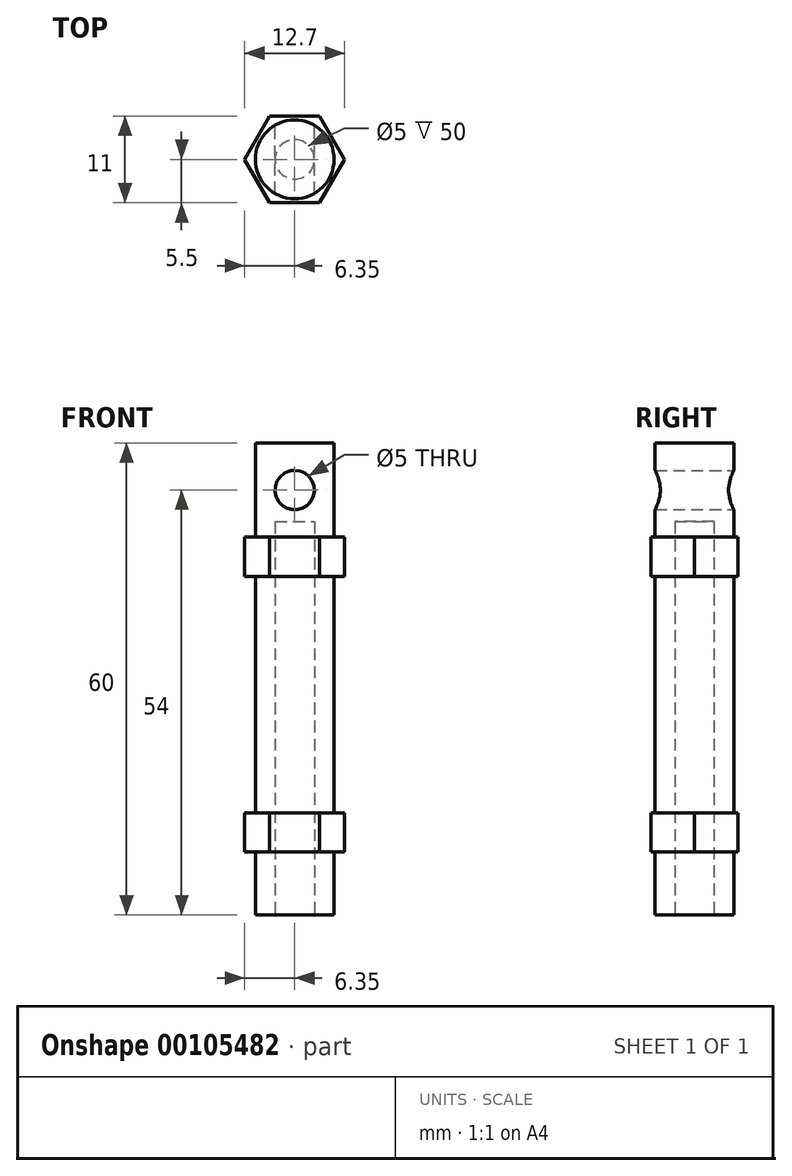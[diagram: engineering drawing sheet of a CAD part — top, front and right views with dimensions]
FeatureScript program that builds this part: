
annotation { "Feature Type Name" : "Feature", "Feature Type Description" : "" }
export const myFeature = defineFeature(function(context is Context, id is Id, definition is map)
    precondition{}
    {
        {
            var Q0;
            Q0=qCreatedBy(makeId("Top.planeOp"),FACE);
            var sketch = newSketch(context, id + "F0", { "sketchPlane" : qUnion([Q0])});
            skCircle(sketch, "E0", {"center": v(0, 0) * mm, "radius": 5 * mm});
            skSolve(sketch);
        }
        {
            var Q0;
            Q0=makeQuery(id+"F0.imprint","IMPRINT",FACE,{"disambiguationData":[TD([[makeQuery(id+"F0.imprint","IMPRINT",EDGE,{"derivedFrom":sQuery(id+"F0.wireOp",EDGE,"E0")}),1.0]])]});
            extrude(context, id + "F1", {"entities" : qUnion([Q0]), "depth" : 60 * mm});
        }
        {
            var Q0;
            Q0=qCreatedBy(makeId("Top.planeOp"),FACE);
            cPlane(context, id + "F2", {"entities" : qUnion([Q0]), "cplaneType" : CPlaneType.OFFSET, "offset" : 8 * mm, "width" : 150 * mm, "height" : 150 * mm});
        }
        {
            var Q0;
            Q0=qCreatedBy(id+"F2.planeOp",FACE);
            var sketch = newSketch(context, id + "F3", { "sketchPlane" : qUnion([Q0])});
            skCircle(sketch, "E1.cCircle", {"center": v(0, 0) * mm, "radius": 5.5 * mm, "construction": true});
            skLineSegment(sketch, "E1.0", {"start": v(-3.18, 5.5) * mm, "end": v(3.18, 5.5) * mm});
            skLineSegment(sketch, "E1.1", {"start": v(3.18, 5.5) * mm, "end": v(6.35, 0) * mm});
            skLineSegment(sketch, "E1.2", {"start": v(6.35, 0) * mm, "end": v(3.18, -5.5) * mm});
            skLineSegment(sketch, "E1.3", {"start": v(3.18, -5.5) * mm, "end": v(-3.18, -5.5) * mm});
            skLineSegment(sketch, "E1.4", {"start": v(-3.18, -5.5) * mm, "end": v(-6.35, 0) * mm});
            skLineSegment(sketch, "E1.5", {"start": v(-6.35, 0) * mm, "end": v(-3.18, 5.5) * mm});
            skPoint(sketch, "E1.0.midPoint", {"position": v(0, 5.5) * mm});
            skSolve(sketch);
        }
        {
            var Q0;
            Q0=makeQuery(id+"F3.imprint","IMPRINT",FACE,{"disambiguationData":[TD([[makeQuery(id+"F3.imprint","IMPRINT",EDGE,{"derivedFrom":sQuery(id+"F3.wireOp",EDGE,"E1.0")}),-1.0]])]});
            extrude(context, id + "F4", {"entities" : qUnion([Q0]), "operationType" : NewBodyOperationType.ADD, "depth" : 5 * mm});
        }
        {
            var Q0;
            Q0=qCreatedBy(id+"F2.planeOp",FACE);
            cPlane(context, id + "F5", {"entities" : qUnion([Q0]), "cplaneType" : CPlaneType.OFFSET, "offset" : 35 * mm, "width" : 150 * mm, "height" : 150 * mm});
        }
        {
            var Q0;
            Q0=qCreatedBy(id+"F5.planeOp",FACE);
            var sketch = newSketch(context, id + "F6", { "sketchPlane" : qUnion([Q0])});
            skCircle(sketch, "E2.cCircle", {"center": v(0, 0) * mm, "radius": 5.5 * mm, "construction": true});
            skLineSegment(sketch, "E2.0", {"start": v(-3.18, 5.5) * mm, "end": v(3.18, 5.5) * mm});
            skLineSegment(sketch, "E2.1", {"start": v(3.18, 5.5) * mm, "end": v(6.35, 0) * mm});
            skLineSegment(sketch, "E2.2", {"start": v(6.35, 0) * mm, "end": v(3.18, -5.5) * mm});
            skLineSegment(sketch, "E2.3", {"start": v(3.18, -5.5) * mm, "end": v(-3.18, -5.5) * mm});
            skLineSegment(sketch, "E2.4", {"start": v(-3.18, -5.5) * mm, "end": v(-6.35, 0) * mm});
            skLineSegment(sketch, "E2.5", {"start": v(-6.35, 0) * mm, "end": v(-3.18, 5.5) * mm});
            skPoint(sketch, "E2.0.midPoint", {"position": v(0, 5.5) * mm});
            skSolve(sketch);
        }
        {
            var Q0;
            Q0=makeQuery(id+"F6.imprint","IMPRINT",FACE,{"disambiguationData":[TD([[makeQuery(id+"F6.imprint","IMPRINT",EDGE,{"derivedFrom":sQuery(id+"F6.wireOp",EDGE,"E2.0")}),-1.0]])]});
            extrude(context, id + "F7", {"entities" : qUnion([Q0]), "operationType" : NewBodyOperationType.ADD, "depth" : 5 * mm});
        }
        {
            var Q0;
            Q0=qCreatedBy(makeId("Front.planeOp"),FACE);
            var sketch = newSketch(context, id + "F8", { "sketchPlane" : qUnion([Q0])});
            skCircle(sketch, "E3", {"center": v(0, 54) * mm, "radius": 2.5 * mm});
            skSolve(sketch);
        }
        {
            var Q0;
            Q0=qSketchRegion(id+"F8",true);
            extrude(context, id + "F9", {"entities" : qUnion([Q0]), "operationType" : NewBodyOperationType.REMOVE, "endBound" : BoundingType.SYMMETRIC, "depth" : 25 * mm});
        }
        {
            var Q0;
            Q0=makeQuery(id+"F1.opExtrude","CAP_FACE",FACE,{"disambiguationData":[OSD([sQuery(id+"F0.wireOp",EDGE,"E0")])],"isStart":true});
            var sketch = newSketch(context, id + "F10", { "sketchPlane" : qUnion([Q0])});
            skCircle(sketch, "E4", {"center": v(0, 0) * mm, "radius": 2.5 * mm});
            skSolve(sketch);
        }
        {
            var Q0;
            Q0=makeQuery(id+"F10.imprint","IMPRINT",FACE,{"disambiguationData":[TD([[makeQuery(id+"F10.imprint","IMPRINT",EDGE,{"derivedFrom":sQuery(id+"F10.wireOp",EDGE,"E4")}),1.0]])]});
            extrude(context, id + "F11", {"entities" : qUnion([Q0]), "operationType" : NewBodyOperationType.REMOVE, "oppositeDirection" : true, "depth" : 50 * mm});
        }
    });
